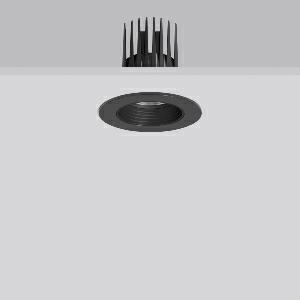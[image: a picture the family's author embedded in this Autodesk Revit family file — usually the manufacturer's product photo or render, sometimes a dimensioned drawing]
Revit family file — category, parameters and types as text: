
# Revit family: heledon_mini_e_901743_003_76_085f
name_source: partatom
category: Lighting Fixtures
units: mm (PartAtom-declared; Revit-internal decimal feet)

## family parameters
Cut with Voids When Loaded = No
Host = Face
Light Source = No
Part Type = Normal
Room Calculation Point = No
Round Connector Dimension = Use Diameter
Shared = No

## types (1)
- HELEDON mini E (1 x LED Modul 930, 2250 lm, 3000)
    Apparent Load = 20 VA
    Approval mark = CE
    CIE Flux Codes = 99 100 100 100 100
    Color Rendering = 90
    Color Temperature = 3000
    Default Elevation = 1800 mm
    Description = Series: HELEDON mini
Round recessed downlight. Housing: die-cast aluminium, powder-coated. Black plastic ring and recessed LED to prevent glare from the side. Optical assembly with lens made of plastic (polycarbonate) for the best homogeneous light distribution - can be changed without tools. Best colour rendering index Ra>90. Suitable for Recessed ceiling mounting. Installation without tools thanks to spring fastening system. Including separate LED converter with connecting cable 600 mm.High quality converter without flickering and stroboscopic effect. Through-wiring box (5 pole) available as accessory. The following accessories can be mounted without use of tools: interchangeable lenses, decorative glasses, honeycomb louvre, clear and frosted diffusers, white interchangeable plastic ring. 
Colour: deep black, matt (RAL 9005)
Diameter: 124 mm
Height: 3 mm
Cut-out diameter: 114 mm
Recess height: 170 mm
Luminaire: recess height: 120 mm
Lamp: LED
Socket: without socket
Colour temperature: 3000K
Colour rendering index (CRI): 92
System power: 20 W
Rated luminous flux: 2250 lm
Luminous efficiency: 113 lm/W
Control gear: Converter, dimmable, DALI
Protection class: II
Type of protection: IP 20
    Height = 0 mm  [stored 0 ft]
    Lamp = 1 x LED Modul 930
    Lamp Light Flux = 2250 lm
    Lamp count = 1
    Length = 124 mm  [stored 0.406824 ft]
    Lifetime = 50000 h
    Luminous efficacy = 113 lm/W
    Manufacturer = RZB
    ModVariant = No
    Model = 901743.003.76
    Mounting Place = Ceiling
    Mounting Type = Recessed
    Number of Poles = 1
    OnlyDefault = Yes
    Power Factor = 1
    Product Name = HELEDON mini E
    Product group = Recessed downlights
    ProductGroupID = 402
    Protection Class = Protection class II
    Protection Degree = IP 20
    RLX_Detail_Level = 1
    RLX_Emergency_Light_Flux = 0 lm
    RLX_Emergency_Type = 0
    RLX_Emergency_Type_DB = No
    RlxData = <blob elided: 125513 chars, md5=82a0fe68>
    Socket = socket
    Standby Power = 0 W
    System Light Flux = 2250 lm
    System Power = 20 W
    Type Comments = Product without accessories
    Type Image = 901656.003.jpg
    URL = http://relux.com
    VarID = ---
    Voltage = 230 V
    Voltage Range = 220-240 V
    Weight = 0.00 kg
    Width = 0 mm  [stored 0 ft]

note: [stored X ft] marks values corroborated as IEEE doubles in the binary element streams (Revit-internal decimal feet)

## geometry (parser evidence)
native form markers: Blend x4, Sweep x11
no freeform markers — native parametric forms only
